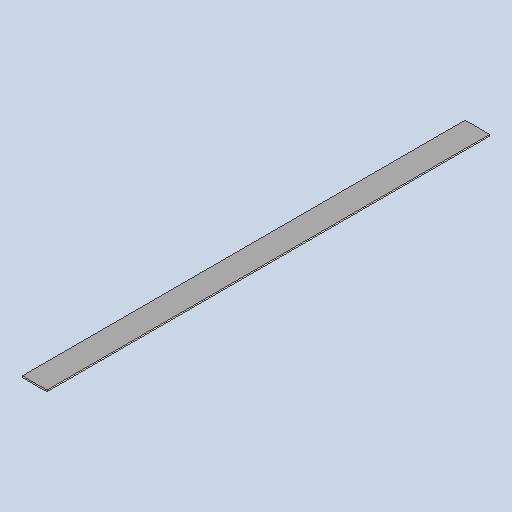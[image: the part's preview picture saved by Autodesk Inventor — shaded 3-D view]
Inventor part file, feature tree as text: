
AUTODESK INVENTOR PART (.ipt)
format: ipt  version: 2025 (Build 290162010, 162A)  size: 111,616 bytes
history: native  units: mm
features: other x3, sheet_metal_op x1, sketch x1
ambient origin geometry x8: Origin, YZ Plane, XZ Plane, XY Plane, X Axis, Y Axis, Z Axis, Center Point
bodies: Body1 (feature_tree)
feature tree (5):
  other  "BSH 503 inner cross"
  sheet_metal_op  "Face2"
  sketch  "Sketch1"  dims[d11=1100.0mm d12=900.0mm d13=25.0mm d14=25.0mm d15=3.0mm]
  other  "Plate2"
  other  "Definition1"
